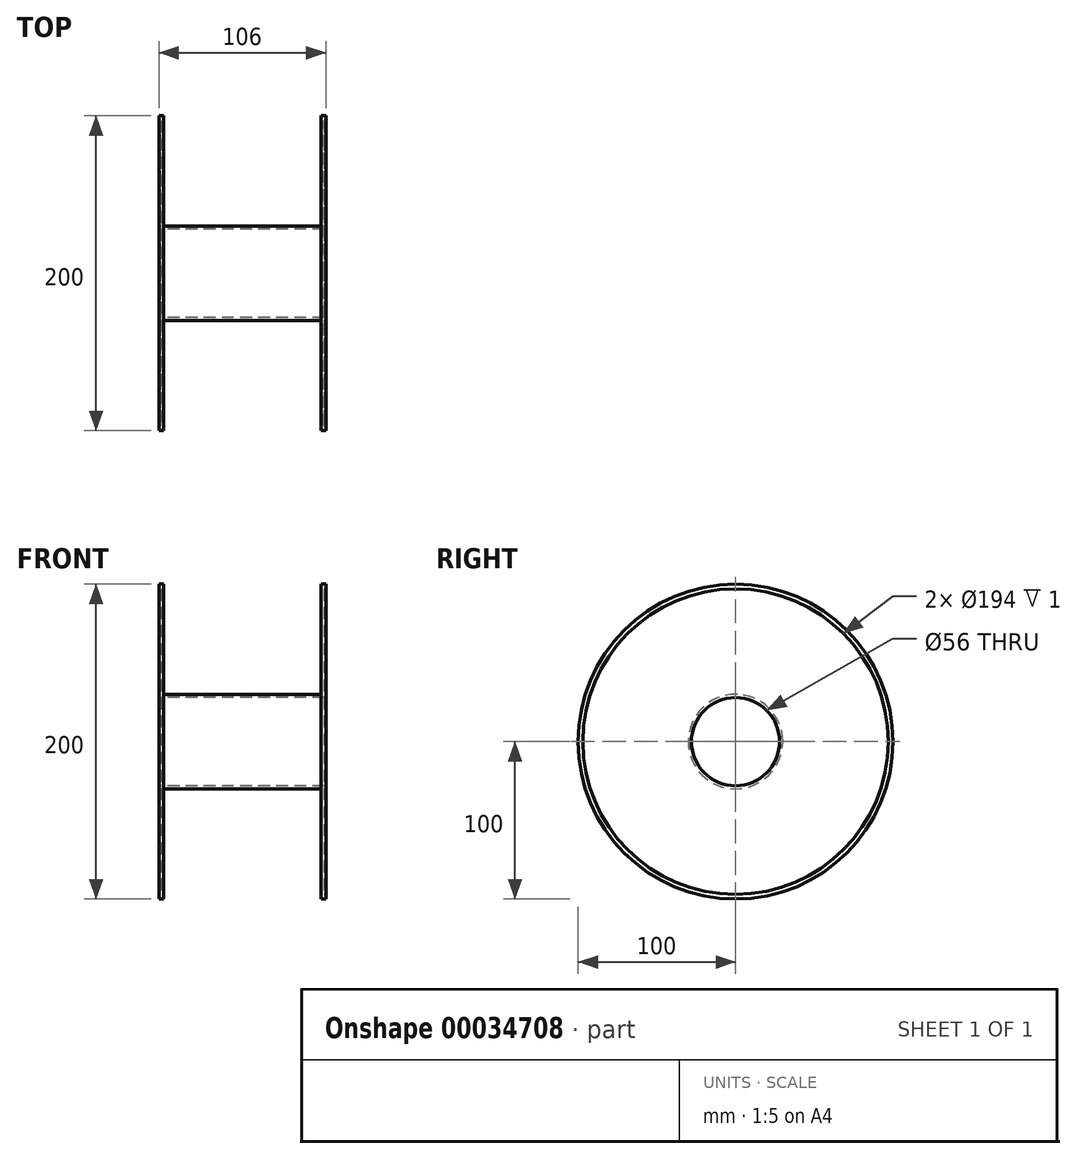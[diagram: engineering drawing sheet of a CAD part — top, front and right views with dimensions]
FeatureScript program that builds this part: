
annotation { "Feature Type Name" : "Feature", "Feature Type Description" : "" }
export const myFeature = defineFeature(function(context is Context, id is Id, definition is map)
    precondition{}
    {
        {
            var Q0;
            Q0=qCreatedBy(makeId("Front.planeOp"),FACE);
            var sketch = newSketch(context, id + "F0", { "sketchPlane" : qUnion([Q0])});
            skLineSegment(sketch, "E0", {"start": v(0, 0) * mm, "end": v(0, 79.22) * mm, "construction": true});
            skLineSegment(sketch, "E1", {"start": v(0, 0) * mm, "end": v(132.96, 0) * mm, "construction": true});
            skLineSegment(sketch, "E2", {"start": v(0, 30) * mm, "end": v(50, 30) * mm});
            skLineSegment(sketch, "E3", {"start": v(50, 30) * mm, "end": v(50, 100) * mm});
            skLineSegment(sketch, "E4", {"start": v(50, 100) * mm, "end": v(53, 100) * mm});
            skLineSegment(sketch, "E5", {"start": v(53, 100) * mm, "end": v(53, 97) * mm});
            skLineSegment(sketch, "E6", {"start": v(53, 97) * mm, "end": v(52, 97) * mm});
            skLineSegment(sketch, "E7", {"start": v(52, 97) * mm, "end": v(52, 28) * mm});
            skLineSegment(sketch, "E8", {"start": v(52, 28) * mm, "end": v(0, 28) * mm});
            skLineSegment(sketch, "E9.MirrorCS", {"start": v(-50, 100) * mm, "end": v(-53, 100) * mm});
            skLineSegment(sketch, "E10.MirrorCS", {"start": v(-53, 100) * mm, "end": v(-53, 97) * mm});
            skLineSegment(sketch, "E11.MirrorCS", {"start": v(-53, 97) * mm, "end": v(-52, 97) * mm});
            skLineSegment(sketch, "E12.MirrorCS", {"start": v(-52, 28) * mm, "end": v(0, 28) * mm});
            skLineSegment(sketch, "E13.MirrorCS", {"start": v(-50, 30) * mm, "end": v(-50, 100) * mm});
            skLineSegment(sketch, "E14.MirrorCS", {"start": v(-52, 97) * mm, "end": v(-52, 28) * mm});
            skLineSegment(sketch, "E15.MirrorCS", {"start": v(0, 30) * mm, "end": v(-50, 30) * mm});
            skSolve(sketch);
        }
        {
            var Q0;
            Q0=makeQuery(id+"F0.imprint","IMPRINT",FACE,{"disambiguationData":[TD([[makeQuery(id+"F0.imprint","IMPRINT",EDGE,{"derivedFrom":sQuery(id+"F0.wireOp",EDGE,"E2")}),-1.0]])]});
            var Q1;
            Q1=sQuery(id+"F0.wireOp",EDGE,"E1");
            revolve(context, id + "F1", {"entities" : qUnion([Q0]), "axis" : qUnion([Q1]), "revolveType" : RevolveType.FULL});
        }
    });
